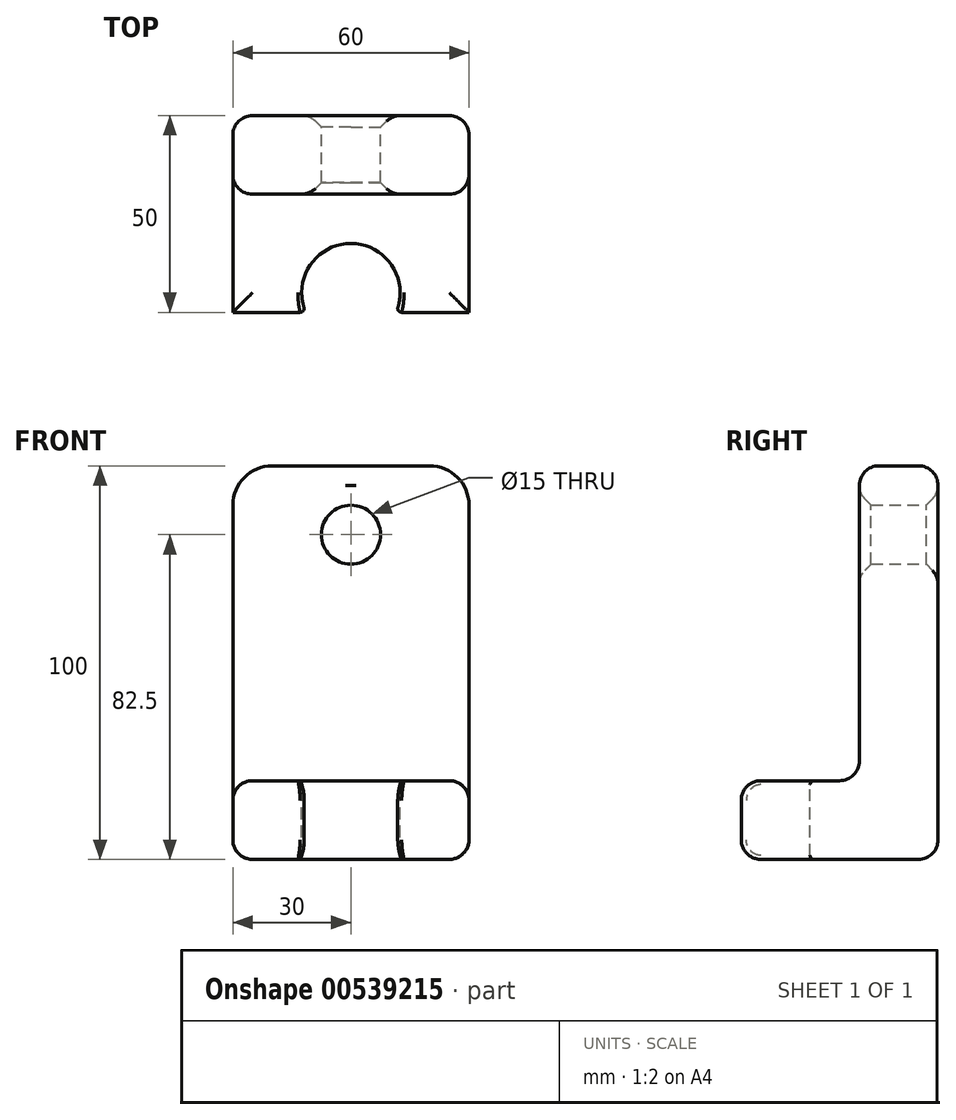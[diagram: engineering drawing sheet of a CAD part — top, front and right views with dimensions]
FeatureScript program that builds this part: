
annotation { "Feature Type Name" : "Feature", "Feature Type Description" : "" }
export const myFeature = defineFeature(function(context is Context, id is Id, definition is map)
    precondition{}
    {
        {
            var Q0;
            Q0=qCreatedBy(makeId("Front.planeOp"),FACE);
            var sketch = newSketch(context, id + "F0", { "sketchPlane" : qUnion([Q0])});
            skLineSegment(sketch, "E0.bottom", {"start": v(-20, 50) * mm, "end": v(20, 50) * mm});
            skLineSegment(sketch, "E0.top", {"start": v(-30, -50) * mm, "end": v(30, -50) * mm});
            skLineSegment(sketch, "E0.left", {"start": v(-30, 40) * mm, "end": v(-30, -50) * mm});
            skLineSegment(sketch, "E0.right", {"start": v(30, 40) * mm, "end": v(30, -50) * mm});
            skPoint(sketch, "E0.middle", {"position": v(0, 0) * mm});
            skLineSegment(sketch, "E1", {"start": v(0, 50) * mm, "end": v(0, -50) * mm, "construction": true});
            skCircle(sketch, "E2", {"center": v(0, 32.5) * mm, "radius": 7.5 * mm});
            skPoint(sketch, "E3.visualSharp", {"position": v(-30, 50) * mm});
            skArc(sketch, "E3.filletArc", {"start": v(-20, 50) * mm, "mid": v(-27.07, 47.07) * mm, "end": v(-30, 40) * mm});
            skPoint(sketch, "E4.visualSharp", {"position": v(30, 50) * mm});
            skArc(sketch, "E4.filletArc", {"start": v(30, 40) * mm, "mid": v(27.07, 47.07) * mm, "end": v(20, 50) * mm});
            skSolve(sketch);
        }
        {
            var Q0;
            Q0=makeQuery(id+"F0.imprint","IMPRINT",FACE,{"disambiguationData":[TD([[makeQuery(id+"F0.imprint","IMPRINT",EDGE,{"derivedFrom":sQuery(id+"F0.wireOp",EDGE,"E0.bottom")}),-1.0]])]});
            extrude(context, id + "F1", {"entities" : qUnion([Q0]), "depth" : 20 * mm, "offsetDistance" : 25 * mm});
        }
        {
            var Q0;
            Q0=makeQuery(id+"F1.opExtrude","SWEPT_FACE",FACE,{"disambiguationData":[OSD([sQuery(id+"F0.wireOp",EDGE,"E2")])]});
            chamfer(context, id + "F2", {"entities" : qUnion([Q0]), "width" : 3 * mm, "tangentPropagation" : true});
        }
        {
            var Q0;
            Q0=makeQuery(id+"F1.opExtrude","CAP_FACE",FACE,{"disambiguationData":[OSD([sQuery(id+"F0.wireOp",EDGE,"E0.bottom"),sQuery(id+"F0.wireOp",EDGE,"E0.top"),sQuery(id+"F0.wireOp",EDGE,"E0.left"),sQuery(id+"F0.wireOp",EDGE,"E0.right"),sQuery(id+"F0.wireOp",EDGE,"E2"),sQuery(id+"F0.wireOp",EDGE,"E3.filletArc"),sQuery(id+"F0.wireOp",EDGE,"E4.filletArc")])],"isStart":false});
            var sketch = newSketch(context, id + "F3", { "sketchPlane" : qUnion([Q0])});
            skLineSegment(sketch, "E5.bottom", {"start": v(-30, -30) * mm, "end": v(30, -30) * mm});
            skLineSegment(sketch, "E5.top", {"start": v(-30, -50) * mm, "end": v(30, -50) * mm});
            skLineSegment(sketch, "E5.left", {"start": v(-30, -30) * mm, "end": v(-30, -50) * mm});
            skLineSegment(sketch, "E5.right", {"start": v(30, -30) * mm, "end": v(30, -50) * mm});
            skSolve(sketch);
        }
        {
            var Q0;
            Q0=makeQuery(id+"F3.imprint","IMPRINT",FACE,{"disambiguationData":[TD([[makeQuery(id+"F3.imprint","IMPRINT",EDGE,{"derivedFrom":sQuery(id+"F3.wireOp",EDGE,"E5.bottom")}),-1.0]])]});
            extrude(context, id + "F4", {"entities" : qUnion([Q0]), "operationType" : NewBodyOperationType.ADD, "depth" : 30 * mm, "offsetDistance" : 25 * mm});
        }
        {
            var Q0;
            Q0=makeQuery(id+"F1.opExtrude","CAP_FACE",FACE,{"disambiguationData":[OSD([sQuery(id+"F0.wireOp",EDGE,"E0.bottom"),sQuery(id+"F0.wireOp",EDGE,"E0.top"),sQuery(id+"F0.wireOp",EDGE,"E0.left"),sQuery(id+"F0.wireOp",EDGE,"E0.right"),sQuery(id+"F0.wireOp",EDGE,"E2"),sQuery(id+"F0.wireOp",EDGE,"E3.filletArc"),sQuery(id+"F0.wireOp",EDGE,"E4.filletArc")])],"isStart":false});
            var Q1;
            Q1=makeQuery(id+"F4.opExtrude","SWEPT_FACE",FACE,{"disambiguationData":[OSD([sQuery(id+"F3.wireOp",EDGE,"E5.bottom")])]});
            fillet(context, id + "F5", {"entities" : qUnion([Q0, Q1]), "radius" : 5 * mm, "tangentPropagation" : true, "allowEdgeOverflow" : false});
        }
        {
            var Q0;
            Q0=makeQuery(id+"F1.opExtrude","CAP_FACE",FACE,{"disambiguationData":[OSD([sQuery(id+"F0.wireOp",EDGE,"E0.bottom"),sQuery(id+"F0.wireOp",EDGE,"E0.top"),sQuery(id+"F0.wireOp",EDGE,"E0.left"),sQuery(id+"F0.wireOp",EDGE,"E0.right"),sQuery(id+"F0.wireOp",EDGE,"E2"),sQuery(id+"F0.wireOp",EDGE,"E3.filletArc"),sQuery(id+"F0.wireOp",EDGE,"E4.filletArc")])],"isStart":true});
            var Q1;
            Q1=makeQuery(id+"F4.boolean.opBoolean","MERGE",FACE,{"derivedFrom":[makeQuery(id+"F1.opExtrude","SWEPT_FACE",FACE,{"disambiguationData":[OSD([sQuery(id+"F0.wireOp",EDGE,"E0.top")])]}),makeQuery(id+"F4.opExtrude","SWEPT_FACE",FACE,{"disambiguationData":[OSD([sQuery(id+"F3.wireOp",EDGE,"E5.top")])]})]});
            fillet(context, id + "F6", {"entities" : qUnion([Q0, Q1]), "radius" : 5 * mm, "tangentPropagation" : true, "allowEdgeOverflow" : false});
        }
        {
            var Q0;
            Q0=makeQuery(id+"F4.opExtrude","SWEPT_FACE",FACE,{"disambiguationData":[OSD([sQuery(id+"F3.wireOp",EDGE,"E5.bottom")])]});
            var sketch = newSketch(context, id + "F7", { "sketchPlane" : qUnion([Q0])});
            skCircle(sketch, "E6", {"center": v(0, -45) * mm, "radius": 12.5 * mm});
            skSolve(sketch);
        }
        {
            var Q0;
            {var subQ0=sQuery(id+"F7.wireOp",EDGE,"E6");var subQ1=sQuery(id+"F3.wireOp",EDGE,"E5.bottom");var subQ2=makeQuery(id+"F5.opFillet","BLEND_EDGE",EDGE,{"blendedFrom":[makeQuery(id+"F4.opExtrude","CAP_EDGE",EDGE,{"disambiguationData":[OSD([subQ1])],"isStart":false}),makeQuery(id+"F4.opExtrude","SWEPT_FACE",FACE,{"disambiguationData":[OSD([subQ1])]})],"blendedInto":[makeQuery(id+"F4.opExtrude","SWEPT_FACE",FACE,{"disambiguationData":[OSD([subQ1])]})]});var subQ3=makeQuery(id+"F7.imprint","INTERSECT",VERTEX,{"disambiguationData":[OD(0.0)],"derivedFrom":[subQ2,subQ0]});Q0=makeQuery(id+"F7.imprint","IMPRINT",FACE,{"disambiguationData":[TD([[makeQuery(id+"F7.imprint","IMPRINT",EDGE,{"disambiguationData":[TD([[subQ3,1.0]])],"derivedFrom":subQ0}),1.0]])]});}
            var Q1;
            {var subQ0=sQuery(id+"F7.wireOp",EDGE,"E6");var subQ1=sQuery(id+"F3.wireOp",EDGE,"E5.bottom");var subQ2=makeQuery(id+"F5.opFillet","BLEND_EDGE",EDGE,{"blendedFrom":[makeQuery(id+"F4.opExtrude","CAP_EDGE",EDGE,{"disambiguationData":[OSD([subQ1])],"isStart":false}),makeQuery(id+"F4.opExtrude","SWEPT_FACE",FACE,{"disambiguationData":[OSD([subQ1])]})],"blendedInto":[makeQuery(id+"F4.opExtrude","SWEPT_FACE",FACE,{"disambiguationData":[OSD([subQ1])]})]});var subQ3=makeQuery(id+"F7.imprint","INTERSECT",VERTEX,{"disambiguationData":[OD(0.0)],"derivedFrom":[subQ2,subQ0]});Q1=makeQuery(id+"F7.imprint","IMPRINT",FACE,{"disambiguationData":[TD([[makeQuery(id+"F7.imprint","IMPRINT",EDGE,{"disambiguationData":[TD([[subQ3,-1.0]])],"derivedFrom":subQ0}),1.0]])]});}
            extrude(context, id + "F8", {"entities" : qUnion([Q0, Q1]), "operationType" : NewBodyOperationType.REMOVE, "endBound" : BoundingType.THROUGH_ALL, "oppositeDirection" : true, "depth" : 25 * mm, "offsetDistance" : 25 * mm});
        }
        {
            var Q0;
            Q0=makeQuery(id+"F8.boolean.opBoolean","COPY",FACE,{"derivedFrom":makeQuery(id+"F8.opExtrude","SWEPT_FACE",FACE,{"disambiguationData":[OSD([sQuery(id+"F7.wireOp",EDGE,"E6")])]})});
            fillet(context, id + "F9", {"entities" : qUnion([Q0]), "radius" : 1 * mm, "tangentPropagation" : true, "allowEdgeOverflow" : false});
        }
    });
